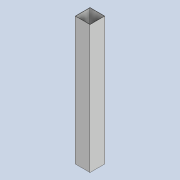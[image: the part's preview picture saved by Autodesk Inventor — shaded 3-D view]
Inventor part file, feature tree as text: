
AUTODESK INVENTOR PART (.ipt)
format: ipt  version: 2021 (Build 250183000, 183)  size: 81,920 bytes
history: native  units: mm
features: other x1, extrude x1, sketch x1
ambient origin geometry x8: Origin, YZ Plane, XZ Plane, XY Plane, X Axis, Y Axis, Z Axis, Center Point
bodies: Body1 (feature_tree)
feature tree (3):
  other  "Sólido1"
  extrude  "Extrusión1"  Depth=80.0mm
  sketch  "Boceto1"  dims[d0=80.0mm d1=80.0mm d2=77.0mm d3=77.0mm d4=690.0mm d5=0.0mm]
